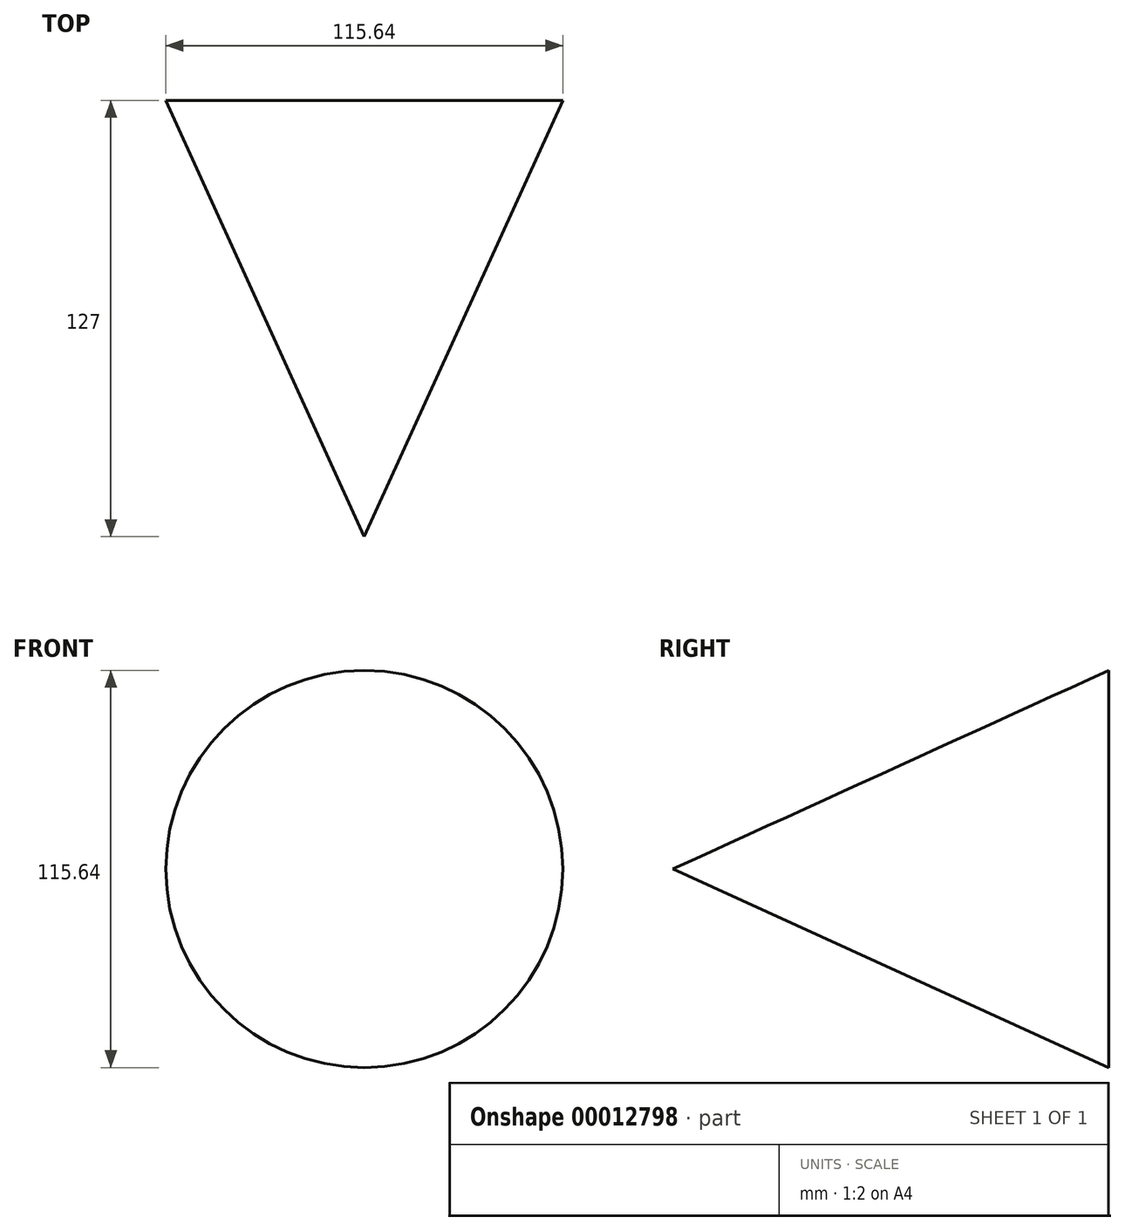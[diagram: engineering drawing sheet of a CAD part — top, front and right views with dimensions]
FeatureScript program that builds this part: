
annotation { "Feature Type Name" : "Feature", "Feature Type Description" : "" }
export const myFeature = defineFeature(function(context is Context, id is Id, definition is map)
    precondition{}
    {
        {
            var Q0;
            Q0=qCreatedBy(makeId("Front.planeOp"),FACE);
            var sketch = newSketch(context, id + "F0", { "sketchPlane" : qUnion([Q0])});
            skCircle(sketch, "E0", {"center": v(0, 52.06) * mm, "radius": 57.82 * mm});
            skSolve(sketch);
        }
        {
            var Q0;
            Q0=makeQuery(id+"F0.imprint","IMPRINT",FACE,{"disambiguationData":[TD([[makeQuery(id+"F0.imprint","IMPRINT",EDGE,{"derivedFrom":sQuery(id+"F0.wireOp",EDGE,"E0")}),1.0]])]});
            cPlane(context, id + "F1", {"entities" : qUnion([Q0]), "cplaneType" : CPlaneType.OFFSET, "offset" : 127 * mm, "width" : 152.4 * mm, "height" : 152.4 * mm});
        }
        {
            var Q0;
            Q0=qCreatedBy(id+"F1.planeOp",FACE);
            var sketch = newSketch(context, id + "F2", { "sketchPlane" : qUnion([Q0])});
            skPoint(sketch, "E1.0", {"position": v(0, 52.06) * mm});
            skCircle(sketch, "E2", {"center": v(0, 52.06) * mm, "radius": 13.6 * mm});
            skSolve(sketch);
        }
        {
            var Q0;
            Q0=makeQuery(id+"F0.imprint","IMPRINT",FACE,{"disambiguationData":[TD([[makeQuery(id+"F0.imprint","IMPRINT",EDGE,{"derivedFrom":sQuery(id+"F0.wireOp",EDGE,"E0")}),1.0]])]});
            var Q1;
            Q1=sQuery(id+"F2.wireOp",VERTEX,"E1.0");
            loft(context, id + "F3", {"sheetProfilesArray" : [{ "sheetProfileEntities" : qUnion([Q0]) }, { "sheetProfileEntities" : qUnion([Q1]) }]});
        }
    });
